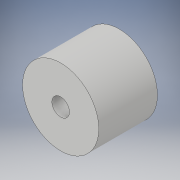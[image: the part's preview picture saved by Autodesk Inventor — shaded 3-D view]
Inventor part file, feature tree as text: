
AUTODESK INVENTOR PART (.ipt)
format: ipt  version: 2019 (Build 230136000, 136)  size: 98,304 bytes
history: native  units: mm
features: extrude x2, sketch x2
ambient origin geometry x8: Origin, YZ Plane, XZ Plane, XY Plane, X Axis, Y Axis, Z Axis, Center Point
bodies: Solid1 (feature_tree)
feature tree (4):
  extrude  "Extrusion1"  Depth=100.0mm TaperAngle=0.0deg
  extrude  "Extrusion2"  Depth=10.0mm TaperAngle=0.0deg
  sketch  "Sketch1"  dims[d0=130.0mm d1=100.0mm d2=0.0mm]
  sketch  "Sketch2"  dims[d3=30.0mm d4=10.0mm d5=0.0mm]
